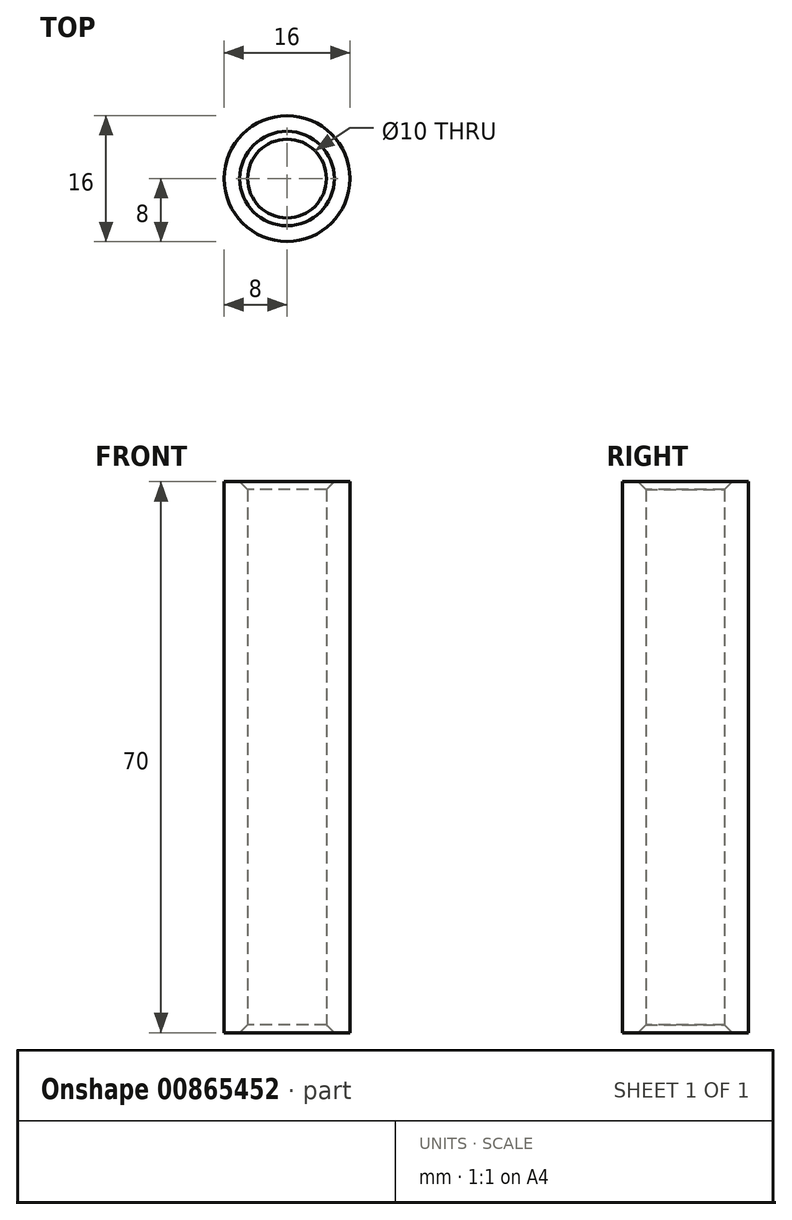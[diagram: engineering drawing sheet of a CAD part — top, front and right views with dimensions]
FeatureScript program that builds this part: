
annotation { "Feature Type Name" : "Feature", "Feature Type Description" : "" }
export const myFeature = defineFeature(function(context is Context, id is Id, definition is map)
    precondition{}
    {
        {
            var Q0;
            Q0=qCreatedBy(makeId("Top.planeOp"),FACE);
            var sketch = newSketch(context, id + "F0", { "sketchPlane" : qUnion([Q0])});
            skCircle(sketch, "E0", {"center": v(0, 0) * mm, "radius": 8 * mm});
            skCircle(sketch, "E1", {"center": v(0, 0) * mm, "radius": 5 * mm});
            skSolve(sketch);
        }
        {
            var Q0;
            Q0 = qSketchRegion(id + "F0", true);
            extrude(context, id + "F1", {"entities" : qUnion([Q0]), "depth" : (70) * mm, "offsetDistance" : 25 * mm});
        }
        {
            var Q0;
            Q0=makeQuery(id+"F1.opExtrude","CAP_EDGE",EDGE,{"disambiguationData":[OSD([sQuery(id+"F0.wireOp",EDGE,"E1")])],"isStart":false});
            var Q1;
            Q1=makeQuery(id+"F1.opExtrude","CAP_EDGE",EDGE,{"disambiguationData":[OSD([sQuery(id+"F0.wireOp",EDGE,"E1")])],"isStart":true});
            chamfer(context, id + "F2", {"entities" : qUnion([Q0, Q1]), "width" : (1) * mm, "tangentPropagation" : true});
        }
    });
